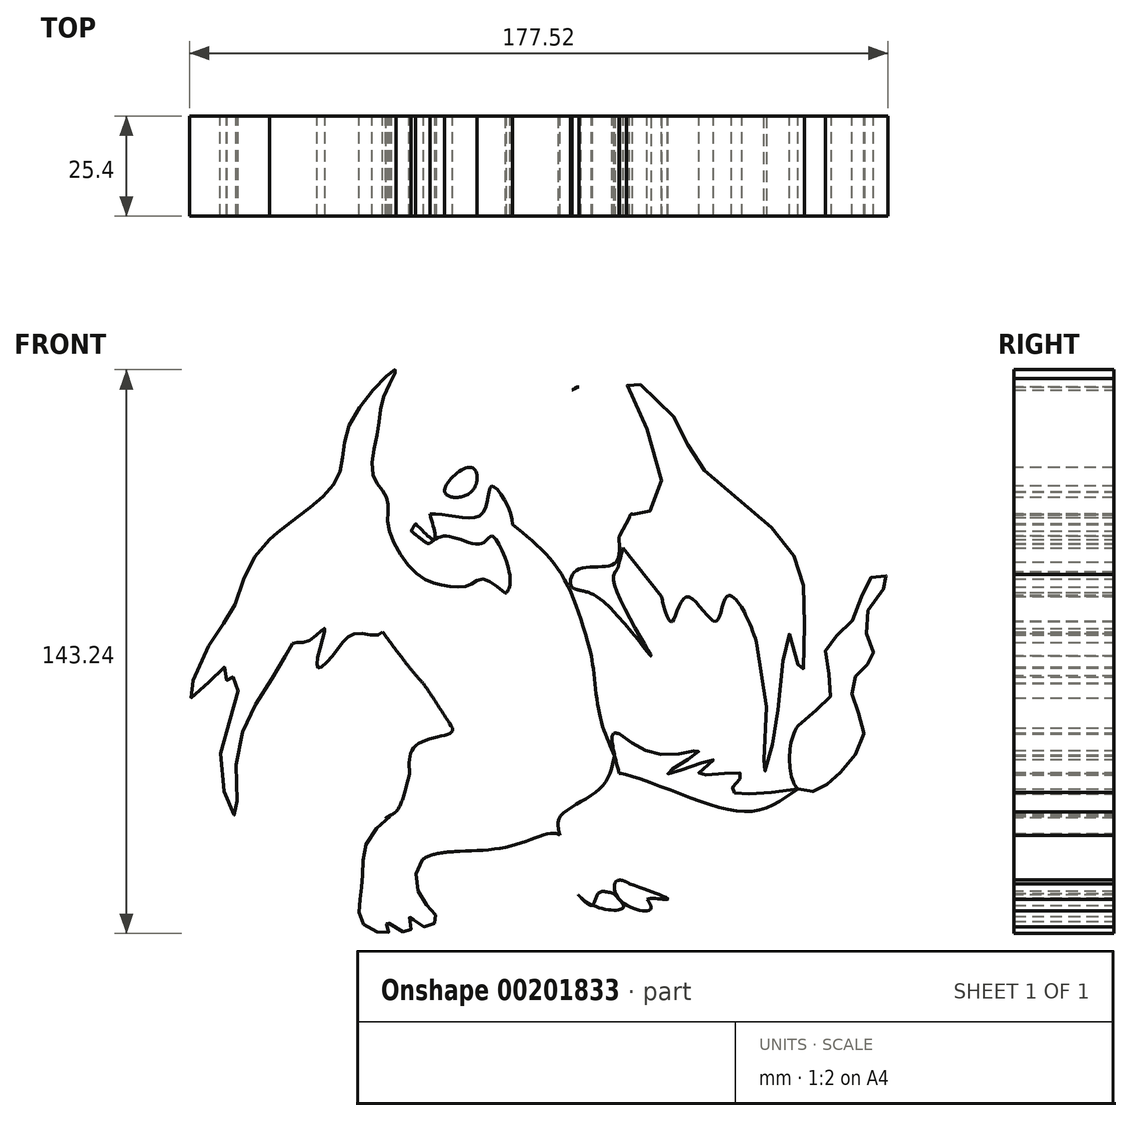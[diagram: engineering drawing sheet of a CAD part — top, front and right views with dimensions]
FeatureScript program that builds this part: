
annotation { "Feature Type Name" : "Feature", "Feature Type Description" : "" }
export const myFeature = defineFeature(function(context is Context, id is Id, definition is map)
    precondition{}
    {
        {
            var Q0;
            Q0=qCreatedBy(makeId("Front.planeOp"),FACE);
            var sketch = newSketch(context, id + "F0", { "sketchPlane" : qUnion([Q0])});
            skArc(sketch, "E0", {"start": v(24.63, 68.4) * mm, "mid": v(10.2, 60.2) * mm, "end": v(-2.66, 49.7) * mm});
            skFitSpline(sketch, "E1", {"points": [v(-2.66, 49.7) * mm, v(-9.46, 47.93) * mm, v(-11.93, 46.8) * mm, v(-13.23, 45.94) * mm, v(-16.43, 41.77) * mm, v(-17.28, 41.61) * mm, v(-20.74, 41.62) * mm, v(-21.88, 39.84) * mm, v(-21.88, 39.9) * mm, v(-21.9, 39.9) * mm], "startDerivative": vector(-35.69, -7.87) * mm, "endDerivative": vector(-2.24, -0.93) * mm});
            skFitSpline(sketch, "E2", {"points": [v(-21.88, 38.23) * mm, v(-21.88, 35.09) * mm, v(-17.99, 31.74) * mm, v(-13.8, 28.6) * mm, v(-13.38, 28.6) * mm], "startDerivative": vector(-2.59, -13.05) * mm, "endDerivative": vector(3.58, 1.17) * mm});
            skFitSpline(sketch, "E3", {"points": [v(-13.38, 28.6) * mm, v(-8.77, 30.48) * mm, v(0, 28.6) * mm, v(2.54, 30.48) * mm, v(7.14, 20) * mm, v(6.1, 15.82) * mm], "startDerivative": vector(21.68, 17.29) * mm, "endDerivative": vector(-11.5, -18.13) * mm});
            skFitSpline(sketch, "E4", {"points": [v(6.1, 15.82) * mm, v(0, 19.6) * mm, v(-3.53, 17.92) * mm, v(-9.19, 17.92) * mm, v(-16.52, 20.85) * mm, v(-23.85, 33.41) * mm, v(-24.06, 39.9) * mm, v(-27.62, 45.98) * mm, v(-26.57, 56.87) * mm, v(-24.69, 66.5) * mm, v(-21.88, 72.78) * mm, v(-33.28, 59.59) * mm, v(-36.63, 45.35) * mm, v(-47.52, 34.88) * mm, v(-54.01, 29.63) * mm], "startDerivative": vector(-105.28, 91.64) * mm, "endDerivative": vector(-83.19, -70.85) * mm});
            skFitSpline(sketch, "E5", {"points": [v(-54.01, 29.63) * mm, v(-59.46, 22.31) * mm, v(-63.44, 11.63) * mm, v(-69.1, 3.26) * mm, v(-74.13, -10.57) * mm, v(-67.42, -4.5) * mm, v(-64.9, -3.03) * mm, v(-64.7, -6.8) * mm, v(-63.23, -5.33) * mm, v(-61.98, -9.3) * mm, v(-66.58, -27.32) * mm, v(-62.6, -40.51) * mm, v(-62.4, -27.32) * mm, v(-56.95, -11.4) * mm, v(-50.03, 0) * mm, v(-48.15, 3.26) * mm, v(-43.96, 3.88) * mm, v(-39.98, 7.03) * mm, v(-41.66, 0) * mm, v(-41.45, -3.03) * mm, v(-36.63, 1.8) * mm, v(-31.6, 5.77) * mm, v(-25.32, 6.19) * mm, v(-30.76, 20) * mm, v(-21.88, 9.96) * mm, v(-15.26, 8.28) * mm, v(-12.09, 10.17) * mm, v(-5.41, 0) * mm, v(-3.74, -3.86) * mm, v(-2.9, 3.47) * mm, v(0, 11.84) * mm, v(7.78, 15.82) * mm, v(9.46, 12.47) * mm, v(9.46, 12.68) * mm], "startDerivative": vector(-179.26, -193.35) * mm, "endDerivative": vector(-3.79, 67.37) * mm});
            skFitSpline(sketch, "E6", {"points": [v(-25.32, 6.19) * mm, v(-15.26, -6.59) * mm, v(-7.72, -11.82) * mm, v(6.1, -17.69) * mm, v(6.1, -19.78) * mm, v(6.1, -23.97) * mm, v(9.46, -21.04) * mm, v(9.46, -24.39) * mm, v(11.34, -22.08) * mm, v(14.07, -22.3) * mm, v(11.76, -19.36) * mm, v(6.1, -10.15) * mm, v(9.46, -4.91) * mm, v(9.46, 10.17) * mm, v(9.46, 12.47) * mm], "startDerivative": vector(93.1, -125.5) * mm, "endDerivative": vector(3.47, 36.3) * mm});
            skLineSegment(sketch, "E7", {"start": v(0, -3.65) * mm, "end": v(5.06, -5.75) * mm});
            skPoint(sketch, "E8.1.internal.snap0", {"position": v(2.53, -4.7) * mm});
            skFitSpline(sketch, "E8", {"points": [v(6.1, -10.15) * mm, v(2.53, -3.65) * mm, v(5.06, 0) * mm, v(5.06, -5.75) * mm, v(5.06, -7.84) * mm], "startDerivative": vector(-18.66, 19.46) * mm, "endDerivative": vector(0.88, -8.85) * mm});
            skFitSpline(sketch, "E9", {"points": [v(-21.73, 1.35) * mm, v(-29.3, 1.35) * mm, v(-39.77, -4.91) * mm, v(-44.38, -10.15) * mm, v(-43.54, -22.5) * mm, v(-31.4, -35.49) * mm, v(-24.48, -41.14) * mm], "startDerivative": vector(-51.43, 8.69) * mm, "endDerivative": vector(40.05, -33.01) * mm});
            skFitSpline(sketch, "E10", {"points": [v(-39.77, -4.91) * mm, v(-41.45, -13.08) * mm, v(-30.55, -26.06) * mm, v(-21.73, -29.41) * mm, v(-20.08, -29.62) * mm, v(-20.08, -30.04) * mm], "startDerivative": vector(-15.2, -31.69) * mm, "endDerivative": vector(-2.23, -8.95) * mm});
            skFitSpline(sketch, "E11", {"points": [v(-18.4, -29.88) * mm, v(-21.73, -39.46) * mm, v(-24.48, -41.14) * mm], "startDerivative": vector(-4.42, -18.29) * mm, "endDerivative": vector(-8.07, -2.8) * mm});
            skFitSpline(sketch, "E12", {"points": [v(-24.48, -41.14) * mm, v(-21.73, -39.46) * mm, v(-28.46, -45.96) * mm, v(-30.34, -56) * mm, v(-31.02, -62.21) * mm, v(-29.69, -68.53) * mm, v(-23.5, -69.9) * mm, v(-24.48, -67.4) * mm, v(-18.4, -70.33) * mm, v(-18.4, -66.14) * mm, v(-15.26, -68.65) * mm, v(-11.54, -66.98) * mm, v(-15.26, -61.53) * mm, v(-15.26, -51.9) * mm, v(6.1, -48.55) * mm, v(19.89, -45.61) * mm, v(24.5, -60.7) * mm, v(35.8, -64.04) * mm, v(33.3, -60.27) * mm], "startDerivative": vector(117.21, 73.55) * mm, "endDerivative": vector(-111.3, 105.3) * mm});
            skFitSpline(sketch, "E13", {"points": [v(24.5, -60.7) * mm, v(28.11, -63.3) * mm, v(29.52, -60.27) * mm, v(33.3, -60.27) * mm], "startDerivative": vector(12.13, -12.79) * mm, "endDerivative": vector(13.65, -3.74) * mm});
            skFitSpline(sketch, "E14", {"points": [v(34.89, -61.78) * mm, v(34.89, -56.92) * mm, v(42.93, -64.04) * mm, v(34.89, -61.78) * mm]});
            skFitSpline(sketch, "E15", {"points": [v(42.93, -64.04) * mm, v(41.94, -61.78) * mm, v(47.12, -61.78) * mm, v(34.89, -56.92) * mm], "startDerivative": vector(-11.14, 13.5) * mm, "endDerivative": vector(-41.04, 14.3) * mm});
            skFitSpline(sketch, "E16", {"points": [v(34.89, -56.92) * mm, v(34.89, -51.06) * mm, v(42.15, -51.9) * mm, v(47.12, -40.8) * mm, v(34.89, -29.88) * mm, v(47.12, -33.78) * mm, v(68.49, -39.46) * mm, v(80.22, -33.78) * mm], "startDerivative": vector(-16.2, 81.24) * mm, "endDerivative": vector(73.62, 53.63) * mm});
            skPoint(sketch, "E17.6.internal.snap0", {"position": v(103.16, 0.1) * mm});
            skFitSpline(sketch, "E17", {"points": [v(80.22, -33.78) * mm, v(85.66, -33.78) * mm, v(90.7, -29.88) * mm, v(96.98, -19.78) * mm, v(94.04, -10.15) * mm, v(96.14, -3.65) * mm, v(99.49, 0.1) * mm, v(97.4, 9.67) * mm, v(103.16, 19.72) * mm, v(99.07, 20.14) * mm, v(94.04, 8.83) * mm, v(87.34, 1.8) * mm, v(88.6, -10.15) * mm, v(80.22, -17.69) * mm, v(80.22, -33.78) * mm]});
            skFitSpline(sketch, "E18", {"points": [v(80.22, -33.78) * mm, v(63.46, -33.78) * mm, v(65.97, -29.88) * mm, v(55.08, -29.88) * mm, v(58.85, -26.35) * mm, v(47.12, -29.88) * mm, v(55.08, -24.25) * mm, v(47.12, -25.1) * mm, v(34.89, -19.78) * mm], "startDerivative": vector(-158.64, -20.03) * mm, "endDerivative": vector(-73.42, 55.1) * mm});
            skFitSpline(sketch, "E19", {"points": [v(34.89, -19.78) * mm, v(33.3, -19.78) * mm, v(34.89, -29.88) * mm], "startDerivative": vector(-6.74, 2) * mm, "endDerivative": vector(5.04, -19.14) * mm});
            skFitSpline(sketch, "E20", {"points": [v(33.68, -25.3) * mm, v(29.94, -15.04) * mm, v(27.85, 0) * mm, v(27.85, 3.81) * mm, v(38.32, -4.14) * mm, v(46.7, -10) * mm, v(50.06, -12.92) * mm, v(50.06, -9.57) * mm, v(52.15, -11.66) * mm, v(50.48, -8.31) * mm, v(53.83, -9.99) * mm, v(49.64, -4.96) * mm], "startDerivative": vector(-36.06, 79.2) * mm, "endDerivative": vector(-82.1, 87.58) * mm});
            skFitSpline(sketch, "E21", {"points": [v(49.64, -4.96) * mm, v(49.64, 5.1) * mm, v(42.1, 23.53) * mm, v(37.9, 36.1) * mm, v(34.89, 23.94) * mm, v(33.68, 18.07) * mm, v(42.93, 0) * mm, v(29.1, 15.13) * mm, v(22.82, 17.64) * mm, v(24.08, 21.83) * mm, v(33.68, 23.51) * mm, v(34.89, 28.6) * mm, v(34.89, 30.48) * mm], "startDerivative": vector(15.57, 114.98) * mm, "endDerivative": vector(1.54, 41.28) * mm});
            skFitSpline(sketch, "E22", {"points": [v(34.89, 30.48) * mm, v(37.9, 36.1) * mm], "startDerivative": vector(3.02, 5.61) * mm, "endDerivative": vector(3.02, 5.61) * mm});
            skFitSpline(sketch, "E23", {"points": [v(37.9, 36.1) * mm, v(41.53, 36.1) * mm, v(45.45, 47.42) * mm, v(36.9, 70.46) * mm, v(49.64, 59.59) * mm, v(53.83, 50.36) * mm, v(69.75, 36.1) * mm, v(80.23, 23.51) * mm, v(81.9, 8.83) * mm, v(81.07, -4.96) * mm, v(78.13, 5.55) * mm, v(75.62, -9.99) * mm, v(73.1, -25.3) * mm, v(71.53, -29.88) * mm, v(71.53, -4.14) * mm, v(62.21, 15.13) * mm, v(59.28, 8.83) * mm, v(52.13, 15.13) * mm, v(48.4, 8.83) * mm, v(45.55, 15.13) * mm], "startDerivative": vector(126.38, -32.3) * mm, "endDerivative": vector(-74.27, 274.25) * mm});
            skFitSpline(sketch, "E24", {"points": [v(22.82, 17.64) * mm, v(18.63, 28.6) * mm, v(7.78, 43.18) * mm, v(13.6, 52) * mm, v(7.78, 50.31) * mm, v(22.82, 67.54) * mm, v(24.63, 68.4) * mm], "startDerivative": vector(-9.12, 62.52) * mm, "endDerivative": vector(14.31, -0.27) * mm});
            skLineSegment(sketch, "E25", {"start": v(-15.26, 1.35) * mm, "end": v(-10.7, -4.61) * mm});
            skLineSegment(sketch, "E26", {"start": v(-3.74, -8.11) * mm, "end": v(6.1, -17.69) * mm});
            skLineSegment(sketch, "E27", {"start": v(0, -8.11) * mm, "end": v(6.1, -17.69) * mm});
            skLineSegment(sketch, "E28", {"start": v(34.89, 28.6) * mm, "end": v(45.55, 15.13) * mm});
            skLineSegment(sketch, "E29", {"start": v(46.5, 11.6) * mm, "end": v(46.5, -1.74) * mm});
            skFitSpline(sketch, "E30", {"points": [v(50.48, 47.42) * mm, v(55.5, 29.83) * mm, v(69.75, 10.99) * mm, v(69.75, 3.48) * mm], "startDerivative": vector(5.78, -48.46) * mm, "endDerivative": vector(-7.95, -30.02) * mm});
            skFitSpline(sketch, "E31", {"points": [v(62.21, 15.13) * mm, v(55.5, 24.8) * mm, v(45.45, 36.1) * mm, v(40.27, 29.83) * mm], "startDerivative": vector(-17.68, 24.64) * mm, "endDerivative": vector(-16.3, -34.3) * mm});
            skFitSpline(sketch, "E32", {"points": [v(19.89, -45.61) * mm, v(34.89, -51.06) * mm], "startDerivative": vector(15, -5.44) * mm, "endDerivative": vector(15, -5.44) * mm});
            skFitSpline(sketch, "E33", {"points": [v(-23.06, -40.25) * mm, v(-15.26, -51.9) * mm], "startDerivative": vector(7.8, -11.65) * mm, "endDerivative": vector(7.8, -11.65) * mm});
            skFitSpline(sketch, "E34", {"points": [v(6.1, -17.69) * mm, v(0, -24.39) * mm, v(0, -40.25) * mm, v(-5.68, -48.55) * mm, v(-6.88, -49.66) * mm], "startDerivative": vector(-30.34, -20.14) * mm, "endDerivative": vector(-8.24, -7.54) * mm});
            skFitSpline(sketch, "E35", {"points": [v(33.68, -25.3) * mm, v(29.89, -33.78) * mm, v(19.89, -40.8) * mm, v(19.89, -45.61) * mm], "startDerivative": vector(-5.36, -26.13) * mm, "endDerivative": vector(6.04, -19.87) * mm});
            skFitSpline(sketch, "E36", {"points": [v(-27.62, 45.98) * mm, v(-30.76, 33.03) * mm, v(-35.85, 15.82) * mm, v(-43.96, 11.6) * mm, v(-48.15, 3.26) * mm], "startDerivative": vector(-12.78, -44.47) * mm, "endDerivative": vector(-13.11, -45.43) * mm});
            skFitSpline(sketch, "E37", {"points": [v(-28.73, 42.1) * mm, v(-24.06, 23.94) * mm, v(0, 11.84) * mm], "startDerivative": vector(2.57, -43.96) * mm, "endDerivative": vector(53.37, -17.36) * mm});
            skFitSpline(sketch, "E38", {"points": [v(-7.72, -17.69) * mm, v(-7.72, -19.36) * mm, v(-16.52, -22.47) * mm, v(-18.4, -29.88) * mm], "startDerivative": vector(4.03, -10.04) * mm, "endDerivative": vector(1.12, -22.34) * mm});
            skFitSpline(sketch, "E39", {"points": [v(-7.47, -18.3) * mm, v(-20.74, -1.74) * mm, v(-21.88, -18.3) * mm, v(-34.18, -11.82) * mm, v(-30.55, -11.82) * mm], "startDerivative": vector(-57.26, 89.91) * mm, "endDerivative": vector(43.4, -9.7) * mm});
            skFitSpline(sketch, "E40", {"points": [v(-30.55, -11.82) * mm, v(-21.88, -11.82) * mm], "startDerivative": vector(8.67, 0) * mm, "endDerivative": vector(8.67, 0) * mm});
            skFitSpline(sketch, "E41", {"points": [v(-17.99, 31.74) * mm, v(-13.23, 36.1) * mm, v(0, 36.1) * mm, v(2.54, 43.18) * mm, v(7.78, 33.41) * mm, v(2.54, 30.48) * mm], "startDerivative": vector(18.55, 34.96) * mm, "endDerivative": vector(-45.49, -5.53) * mm});
            skFitSpline(sketch, "E42", {"points": [v(27.85, 0) * mm, v(19.89, 21.28) * mm, v(7.78, 33.41) * mm], "startDerivative": vector(-11.89, 43.42) * mm, "endDerivative": vector(-28.64, 22.93) * mm});
            skFitSpline(sketch, "E43", {"points": [v(-13.23, 36.1) * mm, v(-12.09, 29.63) * mm, v(-16.92, 33.75) * mm], "startDerivative": vector(5.3, -18.15) * mm, "endDerivative": vector(-12.73, 13.56) * mm});
            skFitSpline(sketch, "E44", {"points": [v(-2.66, 41.77) * mm, v(-9.46, 41.77) * mm, v(-2.66, 47.93) * mm, v(-2.66, 41.77) * mm]});
            skFitSpline(sketch, "E45", {"points": [v(-3.16, 41.91) * mm, v(-1.26, 45.98) * mm], "startDerivative": vector(1.9, 4.06) * mm, "endDerivative": vector(1.9, 4.06) * mm});
            skFitSpline(sketch, "E46", {"points": [v(-1.26, 45.98) * mm, v(-4.86, 44.62) * mm, v(-9.46, 41.77) * mm, v(-2.66, 41.77) * mm], "startDerivative": vector(-10.6, -3.37) * mm, "endDerivative": vector(27, 2.67) * mm});
            skFitSpline(sketch, "E47", {"points": [v(-3.7, 45.12) * mm, v(-2.66, 41.77) * mm], "startDerivative": vector(1.03, -3.35) * mm, "endDerivative": vector(1.03, -3.35) * mm});
            skFitSpline(sketch, "E48", {"points": [v(-35.63, 39.9) * mm, v(-35.37, 29.63) * mm, v(-43.96, 15.13) * mm, v(-58.6, -4.14) * mm, v(-59.39, -4.14) * mm], "startDerivative": vector(6.42, -42.67) * mm, "endDerivative": vector(-9.2, 4.59) * mm});
            skFitSpline(sketch, "E49", {"points": [v(29.1, 15.13) * mm, v(29.1, 18.07) * mm, v(33.68, 21.28) * mm, v(34.89, 23.94) * mm], "startDerivative": vector(-3.04, 10.46) * mm, "endDerivative": vector(1.7, 9.4) * mm});
            skFitSpline(sketch, "E50", {"points": [v(33.68, 21.28) * mm, v(38.32, 23.94) * mm], "startDerivative": vector(4.64, 2.66) * mm, "endDerivative": vector(4.64, 2.66) * mm});
            skFitSpline(sketch, "E51", {"points": [v(55.5, 24.8) * mm, v(41.79, 33.03) * mm, v(40.27, 29.83) * mm, v(42.1, 23.53) * mm], "startDerivative": vector(-35.79, 28.08) * mm, "endDerivative": vector(8.81, -21.17) * mm});
            skFitSpline(sketch, "E52", {"points": [v(80.22, -17.69) * mm, v(80.22, -33.78) * mm], "startDerivative": vector(0, -16.1) * mm, "endDerivative": vector(0, -16.1) * mm});
            skSolve(sketch);
        }
        {
            var Q0;
            {var subQ0=sQuery(id+"F0.wireOp",EDGE,"E52");Q0=makeQuery(id+"F0.imprint","IMPRINT",FACE,{"disambiguationData":[TD([[makeQuery(id+"F0.imprint","IMPRINT",EDGE,{"derivedFrom":subQ0}),-1.0]])]});}
            var Q1;
            {var subQ0=sQuery(id+"F0.wireOp",EDGE,"E18");Q1=makeQuery(id+"F0.imprint","IMPRINT",FACE,{"disambiguationData":[TD([[makeQuery(id+"F0.imprint","IMPRINT",EDGE,{"derivedFrom":subQ0}),1.0]])]});}
            var Q2;
            {var subQ0=sQuery(id+"F0.wireOp",EDGE,"E52");Q2=makeQuery(id+"F0.imprint","IMPRINT",FACE,{"disambiguationData":[TD([[makeQuery(id+"F0.imprint","IMPRINT",EDGE,{"derivedFrom":subQ0}),1.0]])]});}
            var Q3;
            {var subQ0=sQuery(id+"F0.wireOp",EDGE,"E51");var subQ1=sQuery(id+"F0.wireOp",EDGE,"E31");var subQ2=makeQuery(id+"F0.imprint","INTERSECT",VERTEX,{"disambiguationData":[OD(0.0)],"derivedFrom":[subQ1,subQ0]});Q3=makeQuery(id+"F0.imprint","IMPRINT",FACE,{"disambiguationData":[TD([[makeQuery(id+"F0.imprint","IMPRINT",EDGE,{"disambiguationData":[TD([[subQ2,-1.0]])],"derivedFrom":subQ1}),1.0]])]});}
            var Q4;
            {var subQ0=sQuery(id+"F0.wireOp",EDGE,"E15");var subQ1=sQuery(id+"F0.wireOp",EDGE,"E14");var subQ2=makeQuery(id+"F0.imprint","INTERSECT",VERTEX,{"disambiguationData":[OD(2.0)],"derivedFrom":[subQ1,subQ0]});Q4=makeQuery(id+"F0.imprint","IMPRINT",FACE,{"disambiguationData":[TD([[makeQuery(id+"F0.imprint","IMPRINT",EDGE,{"disambiguationData":[TD([[subQ2,-1.0]])],"derivedFrom":subQ1}),-1.0]])]});}
            var Q5;
            {var subQ1=sQuery(id+"F0.wireOp",EDGE,"E23");var subQ5=makeQuery(id+"F0.imprint","IMPRINT",VERTEX,{"derivedFrom":subQ1});Q5=makeQuery(id+"F0.imprint","IMPRINT",FACE,{"disambiguationData":[TD([[makeQuery(id+"F0.imprint","IMPRINT",EDGE,{"disambiguationData":[TD([[subQ5,1.0]])],"derivedFrom":subQ1}),-1.0]])]});}
            var Q6;
            {var subQ1=sQuery(id+"F0.wireOp",EDGE,"E21");var subQ5=sQuery(id+"F0.wireOp",EDGE,"E22");var subQ7=makeQuery(id+"F0.imprint","INTERSECT",VERTEX,{"disambiguationData":[OD(1.0)],"derivedFrom":[subQ1,subQ5]});Q6=makeQuery(id+"F0.imprint","IMPRINT",FACE,{"disambiguationData":[TD([[makeQuery(id+"F0.imprint","IMPRINT",EDGE,{"disambiguationData":[TD([[subQ7,-1.0]])],"derivedFrom":subQ1}),1.0]])]});}
            var Q7;
            {var subQ1=sQuery(id+"F0.wireOp",EDGE,"E31");var subQ5=sQuery(id+"F0.wireOp",EDGE,"E23");var subQ7=makeQuery(id+"F0.imprint","INTERSECT",VERTEX,{"derivedFrom":[subQ5,subQ1]});Q7=makeQuery(id+"F0.imprint","IMPRINT",FACE,{"disambiguationData":[TD([[makeQuery(id+"F0.imprint","IMPRINT",EDGE,{"disambiguationData":[TD([[subQ7,-1.0]])],"derivedFrom":subQ5}),-1.0]])]});}
            var Q8;
            {var subQ1=sQuery(id+"F0.wireOp",EDGE,"E21");var subQ3=sQuery(id+"F0.wireOp",EDGE,"E49");var subQ8=makeQuery(id+"F0.imprint","INTERSECT",VERTEX,{"disambiguationData":[OD(1.0)],"derivedFrom":[subQ1,subQ3]});Q8=makeQuery(id+"F0.imprint","IMPRINT",FACE,{"disambiguationData":[TD([[makeQuery(id+"F0.imprint","IMPRINT",EDGE,{"disambiguationData":[TD([[subQ8,1.0]])],"derivedFrom":subQ1}),-1.0]])]});}
            var Q9;
            {var subQ0=sQuery(id+"F0.wireOp",EDGE,"E12");var subQ1=sQuery(id+"F0.wireOp",EDGE,"E11");var subQ2=makeQuery(id+"F0.imprint","INTERSECT",VERTEX,{"disambiguationData":[OD(2.0)],"derivedFrom":[subQ1,subQ0]});Q9=makeQuery(id+"F0.imprint","IMPRINT",FACE,{"disambiguationData":[TD([[makeQuery(id+"F0.imprint","IMPRINT",EDGE,{"disambiguationData":[TD([[subQ2,1.0]])],"derivedFrom":subQ1}),1.0]])]});}
            var Q10;
            {var subQ4=sQuery(id+"F0.wireOp",EDGE,"E34");Q10=makeQuery(id+"F0.imprint","IMPRINT",FACE,{"disambiguationData":[TD([[makeQuery(id+"F0.imprint","IMPRINT",EDGE,{"derivedFrom":subQ4}),1.0]])]});}
            var Q11;
            {var subQ0=sQuery(id+"F0.wireOp",EDGE,"E6");var subQ3=makeQuery(id+"F0.imprint","IMPRINT",VERTEX,{"derivedFrom":subQ0});Q11=makeQuery(id+"F0.imprint","IMPRINT",FACE,{"disambiguationData":[TD([[makeQuery(id+"F0.imprint","IMPRINT",EDGE,{"disambiguationData":[TD([[subQ3,-1.0]])],"derivedFrom":subQ0}),1.0]])]});}
            var Q12;
            {var subQ0=sQuery(id+"F0.wireOp",EDGE,"E36");var subQ1=sQuery(id+"F0.wireOp",EDGE,"E4");var subQ2=makeQuery(id+"F0.imprint","INTERSECT",VERTEX,{"derivedFrom":[subQ1,subQ0]});Q12=makeQuery(id+"F0.imprint","IMPRINT",FACE,{"disambiguationData":[TD([[makeQuery(id+"F0.imprint","IMPRINT",EDGE,{"disambiguationData":[TD([[subQ2,1.0]])],"derivedFrom":subQ1}),1.0]])]});}
            var Q13;
            {var subQ0=sQuery(id+"F0.wireOp",EDGE,"E5");var subQ1=makeQuery(id+"F0.imprint","INTERSECT",VERTEX,{"disambiguationData":[OD(0.0)],"derivedFrom":[subQ0,sQuery(id+"F0.wireOp",EDGE,"E6")]});Q13=makeQuery(id+"F0.imprint","IMPRINT",FACE,{"disambiguationData":[TD([[makeQuery(id+"F0.imprint","IMPRINT",EDGE,{"disambiguationData":[TD([[subQ1,1.0]])],"derivedFrom":subQ0}),1.0]])]});}
            var Q14;
            {var subQ5=sQuery(id+"F0.wireOp",EDGE,"E34");Q14=makeQuery(id+"F0.imprint","IMPRINT",FACE,{"disambiguationData":[TD([[makeQuery(id+"F0.imprint","IMPRINT",EDGE,{"derivedFrom":subQ5}),-1.0]])]});}
            var Q15;
            {var subQ0=sQuery(id+"F0.wireOp",EDGE,"E5");var subQ1=sQuery(id+"F0.wireOp",EDGE,"E4");var subQ2=makeQuery(id+"F0.imprint","INTERSECT",VERTEX,{"disambiguationData":[OD(0.0)],"derivedFrom":[subQ1,subQ0]});Q15=makeQuery(id+"F0.imprint","IMPRINT",FACE,{"disambiguationData":[TD([[makeQuery(id+"F0.imprint","IMPRINT",EDGE,{"disambiguationData":[TD([[subQ2,1.0]])],"derivedFrom":subQ1}),1.0]])]});}
            var Q16;
            {var subQ1=sQuery(id+"F0.wireOp",EDGE,"E2");var subQ7=sQuery(id+"F0.wireOp",EDGE,"E3");var subQ8=makeQuery(id+"F0.imprint","INTERSECT",VERTEX,{"derivedFrom":[subQ1,subQ7]});Q16=makeQuery(id+"F0.imprint","IMPRINT",FACE,{"disambiguationData":[TD([[makeQuery(id+"F0.imprint","IMPRINT",EDGE,{"disambiguationData":[TD([[subQ8,1.0]])],"derivedFrom":subQ1}),1.0]])]});}
            var Q17;
            {var subQ0=sQuery(id+"F0.wireOp",EDGE,"E43");var subQ1=sQuery(id+"F0.wireOp",EDGE,"E41");var subQ2=makeQuery(id+"F0.imprint","INTERSECT",VERTEX,{"disambiguationData":[OD(0.0)],"derivedFrom":[subQ1,subQ0]});Q17=makeQuery(id+"F0.imprint","IMPRINT",FACE,{"disambiguationData":[TD([[makeQuery(id+"F0.imprint","IMPRINT",EDGE,{"disambiguationData":[TD([[subQ2,1.0]])],"derivedFrom":subQ1}),-1.0]])]});}
            var Q18;
            {var subQ0=sQuery(id+"F0.wireOp",EDGE,"E49");var subQ1=sQuery(id+"F0.wireOp",EDGE,"E21");var subQ2=makeQuery(id+"F0.imprint","INTERSECT",VERTEX,{"disambiguationData":[OD(0.0)],"derivedFrom":[subQ1,subQ0]});Q18=makeQuery(id+"F0.imprint","IMPRINT",FACE,{"disambiguationData":[TD([[makeQuery(id+"F0.imprint","IMPRINT",EDGE,{"disambiguationData":[TD([[subQ2,1.0]])],"derivedFrom":subQ1}),-1.0]])]});}
            var Q19;
            {var subQ1=sQuery(id+"F0.wireOp",EDGE,"E46");var subQ4=sQuery(id+"F0.wireOp",EDGE,"E44");var subQ6=makeQuery(id+"F0.imprint","INTERSECT",VERTEX,{"disambiguationData":[OD(0.0)],"derivedFrom":[subQ4,subQ1]});Q19=makeQuery(id+"F0.imprint","IMPRINT",FACE,{"disambiguationData":[TD([[makeQuery(id+"F0.imprint","IMPRINT",EDGE,{"disambiguationData":[TD([[subQ6,-1.0]])],"derivedFrom":subQ4}),-1.0]])]});}
            var Q20;
            {var subQ0=sQuery(id+"F0.wireOp",EDGE,"E13");var subQ1=sQuery(id+"F0.wireOp",EDGE,"E12");var subQ2=makeQuery(id+"F0.imprint","INTERSECT",VERTEX,{"disambiguationData":[OD(0.0)],"derivedFrom":[subQ1,subQ0]});Q20=makeQuery(id+"F0.imprint","IMPRINT",FACE,{"disambiguationData":[TD([[makeQuery(id+"F0.imprint","IMPRINT",EDGE,{"disambiguationData":[TD([[subQ2,1.0]])],"derivedFrom":subQ1}),1.0]])]});}
            var Q21;
            {var subQ0=sQuery(id+"F0.wireOp",EDGE,"E15");var subQ1=sQuery(id+"F0.wireOp",EDGE,"E14");var subQ2=makeQuery(id+"F0.imprint","INTERSECT",VERTEX,{"disambiguationData":[OD(2.0)],"derivedFrom":[subQ1,subQ0]});Q21=makeQuery(id+"F0.imprint","IMPRINT",FACE,{"disambiguationData":[TD([[makeQuery(id+"F0.imprint","IMPRINT",EDGE,{"disambiguationData":[TD([[subQ2,-1.0]])],"derivedFrom":subQ1}),1.0]])]});}
            var Q22;
            {var subQ0=sQuery(id+"F0.wireOp",EDGE,"E51");var subQ1=sQuery(id+"F0.wireOp",EDGE,"E31");var subQ3=makeQuery(id+"F0.imprint","INTERSECT",VERTEX,{"disambiguationData":[OD(1.0)],"derivedFrom":[subQ1,subQ0]});Q22=makeQuery(id+"F0.imprint","IMPRINT",FACE,{"disambiguationData":[TD([[makeQuery(id+"F0.imprint","IMPRINT",EDGE,{"disambiguationData":[TD([[subQ3,-1.0]])],"derivedFrom":subQ1}),-1.0]])]});}
            var Q23;
            {var subQ0=sQuery(id+"F0.wireOp",EDGE,"E51");var subQ1=sQuery(id+"F0.wireOp",EDGE,"E21");var subQ3=makeQuery(id+"F0.imprint","INTERSECT",VERTEX,{"derivedFrom":[subQ1,subQ0]});Q23=makeQuery(id+"F0.imprint","IMPRINT",FACE,{"disambiguationData":[TD([[makeQuery(id+"F0.imprint","IMPRINT",EDGE,{"disambiguationData":[TD([[subQ3,-1.0]])],"derivedFrom":subQ1}),1.0]])]});}
            var Q24;
            {var subQ0=sQuery(id+"F0.wireOp",EDGE,"E22");var subQ1=sQuery(id+"F0.wireOp",EDGE,"E21");var subQ2=makeQuery(id+"F0.imprint","INTERSECT",VERTEX,{"disambiguationData":[OD(1.0)],"derivedFrom":[subQ1,subQ0]});Q24=makeQuery(id+"F0.imprint","IMPRINT",FACE,{"disambiguationData":[TD([[makeQuery(id+"F0.imprint","IMPRINT",EDGE,{"disambiguationData":[TD([[subQ2,-1.0]])],"derivedFrom":subQ1}),-1.0]])]});}
            var Q25;
            {var subQ0=sQuery(id+"F0.wireOp",EDGE,"E8");var subQ1=sQuery(id+"F0.wireOp",EDGE,"E7");var subQ2=makeQuery(id+"F0.imprint","INTERSECT",VERTEX,{"disambiguationData":[OD(0.0)],"derivedFrom":[subQ1,subQ0]});Q25=makeQuery(id+"F0.imprint","IMPRINT",FACE,{"disambiguationData":[TD([[makeQuery(id+"F0.imprint","IMPRINT",EDGE,{"disambiguationData":[TD([[subQ2,1.0]])],"derivedFrom":subQ1}),1.0]])]});}
            var Q26;
            {var subQ0=sQuery(id+"F0.wireOp",EDGE,"E39");var subQ1=sQuery(id+"F0.wireOp",EDGE,"E6");var subQ2=makeQuery(id+"F0.imprint","INTERSECT",VERTEX,{"disambiguationData":[OD(0.0)],"derivedFrom":[subQ1,subQ0]});Q26=makeQuery(id+"F0.imprint","IMPRINT",FACE,{"disambiguationData":[TD([[makeQuery(id+"F0.imprint","IMPRINT",EDGE,{"disambiguationData":[TD([[subQ2,-1.0]])],"derivedFrom":subQ1}),1.0]])]});}
            var Q27;
            {var subQ0=sQuery(id+"F0.wireOp",EDGE,"E24");var subQ1=sQuery(id+"F0.wireOp",EDGE,"E0");var subQ2=makeQuery(id+"F0.imprint","INTERSECT",VERTEX,{"disambiguationData":[OD(0.0)],"derivedFrom":[subQ1,subQ0]});Q27=makeQuery(id+"F0.imprint","IMPRINT",FACE,{"disambiguationData":[TD([[makeQuery(id+"F0.imprint","IMPRINT",EDGE,{"disambiguationData":[TD([[subQ2,-1.0]])],"derivedFrom":subQ1}),-1.0]])]});}
            var Q28;
            {var subQ0=sQuery(id+"F0.wireOp",EDGE,"E23");var subQ1=sQuery(id+"F0.wireOp",EDGE,"E21");var subQ3=makeQuery(id+"F0.imprint","INTERSECT",VERTEX,{"disambiguationData":[OD(0.0)],"derivedFrom":[subQ1,subQ0]});Q28=makeQuery(id+"F0.imprint","IMPRINT",FACE,{"disambiguationData":[TD([[makeQuery(id+"F0.imprint","IMPRINT",EDGE,{"disambiguationData":[TD([[subQ3,-1.0]])],"derivedFrom":subQ1}),1.0]])]});}
            var Q29;
            {var subQ0=sQuery(id+"F0.wireOp",EDGE,"E46");var subQ4=makeQuery(id+"F0.imprint","INTERSECT",VERTEX,{"derivedFrom":[subQ0,sQuery(id+"F0.wireOp",EDGE,"E47")]});Q29=makeQuery(id+"F0.imprint","IMPRINT",FACE,{"disambiguationData":[TD([[makeQuery(id+"F0.imprint","IMPRINT",EDGE,{"disambiguationData":[TD([[subQ4,-1.0]])],"derivedFrom":subQ0}),-1.0]])]});}
            var Q30;
            {var subQ0=sQuery(id+"F0.wireOp",EDGE,"E46");var subQ1=sQuery(id+"F0.wireOp",EDGE,"E44");var subQ3=makeQuery(id+"F0.imprint","INTERSECT",VERTEX,{"disambiguationData":[OD(0.0)],"derivedFrom":[subQ1,subQ0]});Q30=makeQuery(id+"F0.imprint","IMPRINT",FACE,{"disambiguationData":[TD([[makeQuery(id+"F0.imprint","IMPRINT",EDGE,{"disambiguationData":[TD([[subQ3,1.0]])],"derivedFrom":subQ1}),-1.0]])]});}
            var Q31;
            {var subQ0=sQuery(id+"F0.wireOp",EDGE,"E15");var subQ1=sQuery(id+"F0.wireOp",EDGE,"E14");var subQ2=makeQuery(id+"F0.imprint","INTERSECT",VERTEX,{"disambiguationData":[OD(1.0)],"derivedFrom":[subQ1,subQ0]});Q31=makeQuery(id+"F0.imprint","IMPRINT",FACE,{"disambiguationData":[TD([[makeQuery(id+"F0.imprint","IMPRINT",EDGE,{"disambiguationData":[TD([[subQ2,-1.0]])],"derivedFrom":subQ1}),-1.0]])]});}
            var Q32;
            {var subQ0=sQuery(id+"F0.wireOp",EDGE,"E12");var subQ1=sQuery(id+"F0.wireOp",EDGE,"E11");var subQ2=makeQuery(id+"F0.imprint","INTERSECT",VERTEX,{"disambiguationData":[OD(1.0)],"derivedFrom":[subQ1,subQ0]});Q32=makeQuery(id+"F0.imprint","IMPRINT",FACE,{"disambiguationData":[TD([[makeQuery(id+"F0.imprint","IMPRINT",EDGE,{"disambiguationData":[TD([[subQ2,-1.0]])],"derivedFrom":subQ1}),-1.0]])]});}
            var Q33;
            {var subQ0=sQuery(id+"F0.wireOp",EDGE,"E46");var subQ1=sQuery(id+"F0.wireOp",EDGE,"E44");var subQ2=makeQuery(id+"F0.imprint","INTERSECT",VERTEX,{"disambiguationData":[OD(0.0)],"derivedFrom":[subQ1,subQ0]});Q33=makeQuery(id+"F0.imprint","IMPRINT",FACE,{"disambiguationData":[TD([[makeQuery(id+"F0.imprint","IMPRINT",EDGE,{"disambiguationData":[TD([[subQ2,-1.0]])],"derivedFrom":subQ1}),1.0]])]});}
            var Q34;
            {var subQ0=sQuery(id+"F0.wireOp",EDGE,"E13");var subQ1=sQuery(id+"F0.wireOp",EDGE,"E12");var subQ2=makeQuery(id+"F0.imprint","INTERSECT",VERTEX,{"disambiguationData":[OD(2.0)],"derivedFrom":[subQ1,subQ0]});Q34=makeQuery(id+"F0.imprint","IMPRINT",FACE,{"disambiguationData":[TD([[makeQuery(id+"F0.imprint","IMPRINT",EDGE,{"disambiguationData":[TD([[subQ2,-1.0]])],"derivedFrom":subQ1}),-1.0]])]});}
            var Q35;
            {var subQ0=sQuery(id+"F0.wireOp",EDGE,"E15");var subQ1=sQuery(id+"F0.wireOp",EDGE,"E14");var subQ2=makeQuery(id+"F0.imprint","INTERSECT",VERTEX,{"disambiguationData":[OD(0.0)],"derivedFrom":[subQ1,subQ0]});Q35=makeQuery(id+"F0.imprint","IMPRINT",FACE,{"disambiguationData":[TD([[makeQuery(id+"F0.imprint","IMPRINT",EDGE,{"disambiguationData":[TD([[subQ2,1.0]])],"derivedFrom":subQ1}),-1.0]])]});}
            var Q36;
            {var subQ0=sQuery(id+"F0.wireOp",EDGE,"E19");var subQ1=sQuery(id+"F0.wireOp",EDGE,"E16");var subQ2=makeQuery(id+"F0.imprint","INTERSECT",VERTEX,{"disambiguationData":[OD(0.0)],"derivedFrom":[subQ1,subQ0]});Q36=makeQuery(id+"F0.imprint","IMPRINT",FACE,{"disambiguationData":[TD([[makeQuery(id+"F0.imprint","IMPRINT",EDGE,{"disambiguationData":[TD([[subQ2,-1.0]])],"derivedFrom":subQ1}),-1.0]])]});}
            var Q37;
            {var subQ0=sQuery(id+"F0.wireOp",EDGE,"E50");var subQ1=sQuery(id+"F0.wireOp",EDGE,"E21");var subQ2=makeQuery(id+"F0.imprint","INTERSECT",VERTEX,{"derivedFrom":[subQ1,subQ0]});Q37=makeQuery(id+"F0.imprint","IMPRINT",FACE,{"disambiguationData":[TD([[makeQuery(id+"F0.imprint","IMPRINT",EDGE,{"disambiguationData":[TD([[subQ2,1.0]])],"derivedFrom":subQ1}),-1.0]])]});}
            var Q38;
            {var subQ0=sQuery(id+"F0.wireOp",EDGE,"E24");var subQ1=sQuery(id+"F0.wireOp",EDGE,"E21");var subQ2=makeQuery(id+"F0.imprint","INTERSECT",VERTEX,{"disambiguationData":[OD(0.0)],"derivedFrom":[subQ1,subQ0]});Q38=makeQuery(id+"F0.imprint","IMPRINT",FACE,{"disambiguationData":[TD([[makeQuery(id+"F0.imprint","IMPRINT",EDGE,{"disambiguationData":[TD([[subQ2,-1.0]])],"derivedFrom":subQ1}),-1.0]])]});}
            var Q39;
            {var subQ0=sQuery(id+"F0.wireOp",EDGE,"E49");var subQ1=sQuery(id+"F0.wireOp",EDGE,"E21");var subQ2=makeQuery(id+"F0.imprint","INTERSECT",VERTEX,{"disambiguationData":[OD(1.0)],"derivedFrom":[subQ1,subQ0]});Q39=makeQuery(id+"F0.imprint","IMPRINT",FACE,{"disambiguationData":[TD([[makeQuery(id+"F0.imprint","IMPRINT",EDGE,{"disambiguationData":[TD([[subQ2,-1.0]])],"derivedFrom":subQ1}),1.0]])]});}
            var Q40;
            {var subQ0=sQuery(id+"F0.wireOp",EDGE,"E33");var subQ1=sQuery(id+"F0.wireOp",EDGE,"E12");var subQ2=makeQuery(id+"F0.imprint","INTERSECT",VERTEX,{"disambiguationData":[OD(1.0)],"derivedFrom":[subQ1,subQ0]});Q40=makeQuery(id+"F0.imprint","IMPRINT",FACE,{"disambiguationData":[TD([[makeQuery(id+"F0.imprint","IMPRINT",EDGE,{"disambiguationData":[TD([[subQ2,-1.0]])],"derivedFrom":subQ1}),-1.0]])]});}
            var Q41;
            {var subQ0=sQuery(id+"F0.wireOp",EDGE,"E46");var subQ3=sQuery(id+"F0.wireOp",EDGE,"E47");var subQ5=makeQuery(id+"F0.imprint","INTERSECT",VERTEX,{"derivedFrom":[subQ0,subQ3]});Q41=makeQuery(id+"F0.imprint","IMPRINT",FACE,{"disambiguationData":[TD([[makeQuery(id+"F0.imprint","IMPRINT",EDGE,{"disambiguationData":[TD([[subQ5,-1.0]])],"derivedFrom":subQ3}),1.0]])]});}
            var Q42;
            {var subQ0=sQuery(id+"F0.wireOp",EDGE,"E13");var subQ1=sQuery(id+"F0.wireOp",EDGE,"E12");var subQ2=makeQuery(id+"F0.imprint","INTERSECT",VERTEX,{"disambiguationData":[OD(1.0)],"derivedFrom":[subQ1,subQ0]});Q42=makeQuery(id+"F0.imprint","IMPRINT",FACE,{"disambiguationData":[TD([[makeQuery(id+"F0.imprint","IMPRINT",EDGE,{"disambiguationData":[TD([[subQ2,-1.0]])],"derivedFrom":subQ1}),1.0]])]});}
            var Q43;
            {var subQ0=sQuery(id+"F0.wireOp",EDGE,"E4");var subQ1=sQuery(id+"F0.wireOp",EDGE,"E3");var subQ2=makeQuery(id+"F0.imprint","INTERSECT",VERTEX,{"derivedFrom":[subQ1,subQ0]});Q43=makeQuery(id+"F0.imprint","IMPRINT",FACE,{"disambiguationData":[TD([[makeQuery(id+"F0.imprint","IMPRINT",EDGE,{"disambiguationData":[TD([[subQ2,1.0]])],"derivedFrom":subQ1}),-1.0]])]});}
            var Q44;
            {var subQ1=sQuery(id+"F0.wireOp",EDGE,"E45");var subQ4=sQuery(id+"F0.wireOp",EDGE,"E47");var subQ6=makeQuery(id+"F0.imprint","INTERSECT",VERTEX,{"derivedFrom":[subQ1,subQ4]});Q44=makeQuery(id+"F0.imprint","IMPRINT",FACE,{"disambiguationData":[TD([[makeQuery(id+"F0.imprint","IMPRINT",EDGE,{"disambiguationData":[TD([[subQ6,-1.0]])],"derivedFrom":subQ1}),-1.0]])]});}
            var Q45;
            {var subQ0=sQuery(id+"F0.wireOp",EDGE,"E26");var subQ1=sQuery(id+"F0.wireOp",EDGE,"E6");var subQ3=makeQuery(id+"F0.imprint","INTERSECT",VERTEX,{"derivedFrom":[subQ1,subQ0]});Q45=makeQuery(id+"F0.imprint","IMPRINT",FACE,{"disambiguationData":[TD([[makeQuery(id+"F0.imprint","IMPRINT",EDGE,{"disambiguationData":[TD([[subQ3,-1.0]])],"derivedFrom":subQ1}),-1.0]])]});}
            var Q46;
            {var subQ0=sQuery(id+"F0.wireOp",EDGE,"E22");var subQ1=sQuery(id+"F0.wireOp",EDGE,"E21");var subQ3=makeQuery(id+"F0.imprint","INTERSECT",VERTEX,{"disambiguationData":[OD(1.0)],"derivedFrom":[subQ1,subQ0]});Q46=makeQuery(id+"F0.imprint","IMPRINT",FACE,{"disambiguationData":[TD([[makeQuery(id+"F0.imprint","IMPRINT",EDGE,{"disambiguationData":[TD([[subQ3,1.0]])],"derivedFrom":subQ1}),1.0]])]});}
            var Q47;
            {var subQ0=sQuery(id+"F0.wireOp",EDGE,"E12");var subQ1=sQuery(id+"F0.wireOp",EDGE,"E11");var subQ2=makeQuery(id+"F0.imprint","INTERSECT",VERTEX,{"disambiguationData":[OD(0.0)],"derivedFrom":[subQ1,subQ0]});Q47=makeQuery(id+"F0.imprint","IMPRINT",FACE,{"disambiguationData":[TD([[makeQuery(id+"F0.imprint","IMPRINT",EDGE,{"disambiguationData":[TD([[subQ2,1.0]])],"derivedFrom":subQ1}),-1.0]])]});}
            var Q48;
            {var subQ0=sQuery(id+"F0.wireOp",EDGE,"E23");var subQ1=sQuery(id+"F0.wireOp",EDGE,"E21");var subQ3=makeQuery(id+"F0.imprint","INTERSECT",VERTEX,{"disambiguationData":[OD(1.0)],"derivedFrom":[subQ1,subQ0]});Q48=makeQuery(id+"F0.imprint","IMPRINT",FACE,{"disambiguationData":[TD([[makeQuery(id+"F0.imprint","IMPRINT",EDGE,{"disambiguationData":[TD([[subQ3,-1.0]])],"derivedFrom":subQ1}),1.0]])]});}
            var Q49;
            {var subQ0=sQuery(id+"F0.wireOp",EDGE,"E12");var subQ1=sQuery(id+"F0.wireOp",EDGE,"E11");var subQ2=makeQuery(id+"F0.imprint","INTERSECT",VERTEX,{"disambiguationData":[OD(2.0)],"derivedFrom":[subQ1,subQ0]});Q49=makeQuery(id+"F0.imprint","IMPRINT",FACE,{"disambiguationData":[TD([[makeQuery(id+"F0.imprint","IMPRINT",EDGE,{"disambiguationData":[TD([[subQ2,1.0]])],"derivedFrom":subQ1}),-1.0]])]});}
            extrude(context, id + "F1", {"entities" : qUnion([Q0, Q1, Q2, Q3, Q4, Q5, Q6, Q7, Q8, Q9, Q10, Q11, Q12, Q13, Q14, Q15, Q16, Q17, Q18, Q19, Q20, Q21, Q22, Q23, Q24, Q25, Q26, Q27, Q28, Q29, Q30, Q31, Q32, Q33, Q34, Q35, Q36, Q37, Q38, Q39, Q40, Q41, Q42, Q43, Q44, Q45, Q46, Q47, Q48, Q49]), "depth" : 25.4 * mm, "offsetDistance" : 25.4 * mm});
        }
    });
